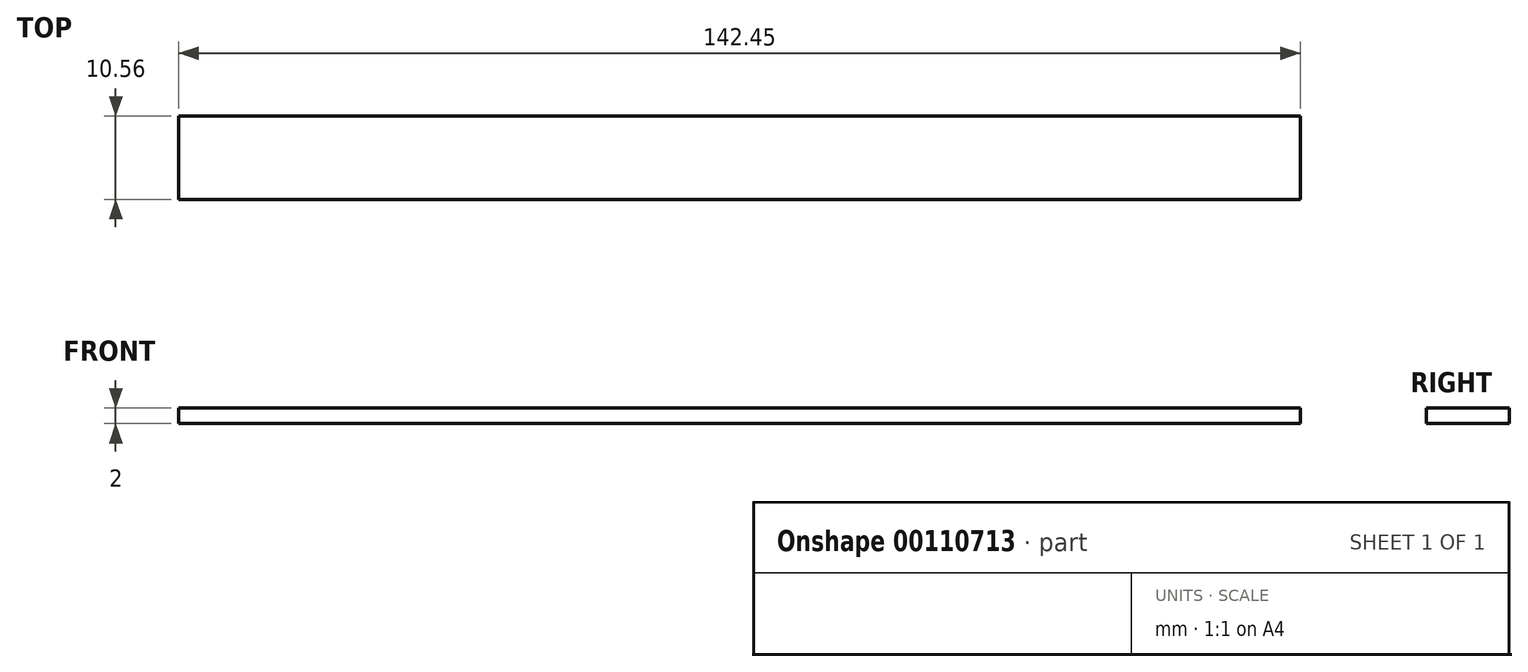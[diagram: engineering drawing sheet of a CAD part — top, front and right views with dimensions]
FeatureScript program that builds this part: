
annotation { "Feature Type Name" : "Feature", "Feature Type Description" : "" }
export const myFeature = defineFeature(function(context is Context, id is Id, definition is map)
    precondition{}
    {
        {
            var Q0;
            Q0=qCreatedBy(makeId("Top.planeOp"),FACE);
            var sketch = newSketch(context, id + "F0", { "sketchPlane" : qUnion([Q0])});
            skLineSegment(sketch, "E0.bottom", {"start": v(-72.3, 7.43) * mm, "end": v(70.15, 7.43) * mm});
            skLineSegment(sketch, "E0.top", {"start": v(-72.3, -3.13) * mm, "end": v(70.15, -3.13) * mm});
            skLineSegment(sketch, "E0.left", {"start": v(-72.3, 7.43) * mm, "end": v(-72.3, -3.13) * mm});
            skLineSegment(sketch, "E0.right", {"start": v(70.15, 7.43) * mm, "end": v(70.15, -3.13) * mm});
            skSolve(sketch);
        }
        {
            var Q0;
            Q0 = qSketchRegion(id + "F0", true);
            extrude(context, id + "F1", {"entities" : qUnion([Q0]), "depth" : 2 * mm});
        }
    });
